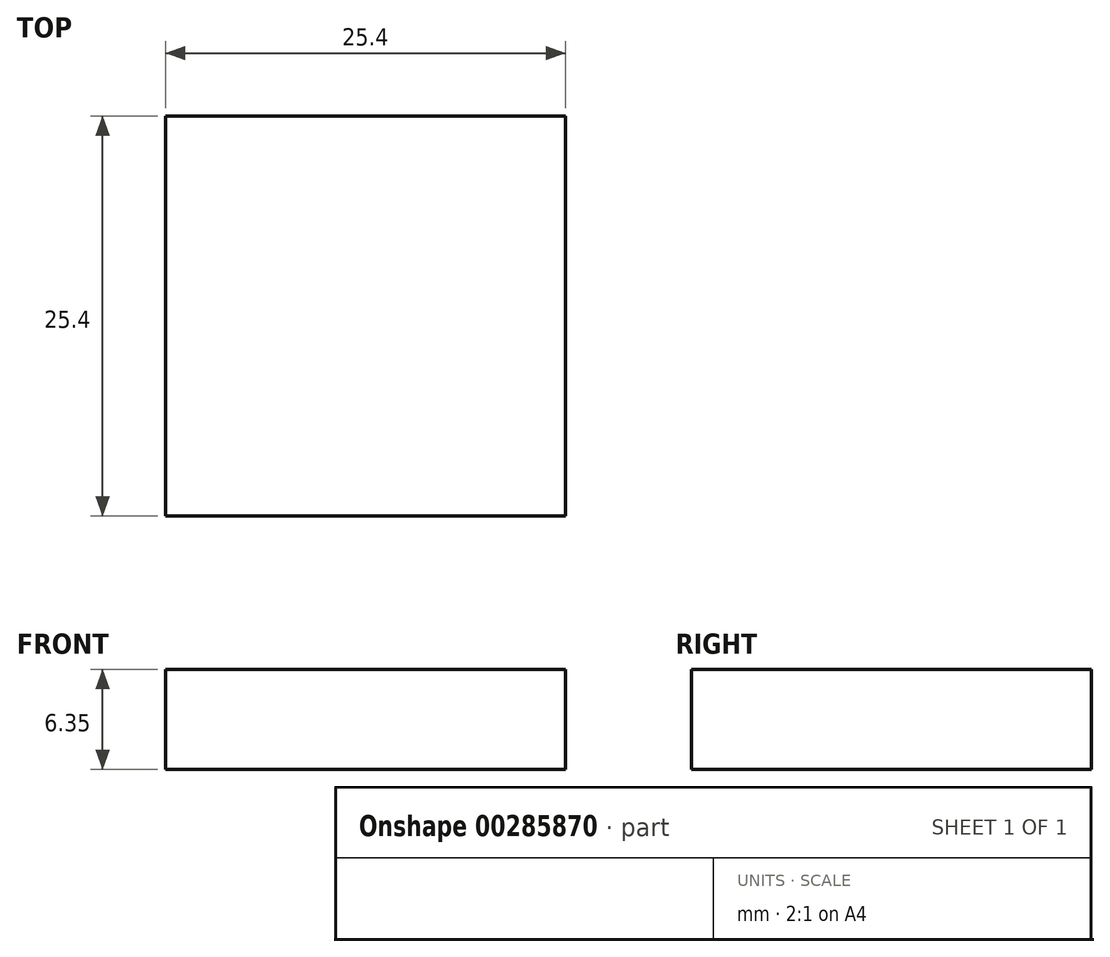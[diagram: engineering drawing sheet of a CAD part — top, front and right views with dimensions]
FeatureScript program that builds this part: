
annotation { "Feature Type Name" : "Feature", "Feature Type Description" : "" }
export const myFeature = defineFeature(function(context is Context, id is Id, definition is map)
    precondition{}
    {
        {
            var Q0;
            Q0=qCreatedBy(makeId("Top.planeOp"),FACE);
            var sketch = newSketch(context, id + "F0", { "sketchPlane" : qUnion([Q0])});
            skLineSegment(sketch, "E0.bottom", {"start": v(0, 0) * mm, "end": v(25.4, 0) * mm});
            skLineSegment(sketch, "E0.top", {"start": v(0, -25.4) * mm, "end": v(25.4, -25.4) * mm});
            skLineSegment(sketch, "E0.left", {"start": v(0, 0) * mm, "end": v(0, -25.4) * mm});
            skLineSegment(sketch, "E0.right", {"start": v(25.4, 0) * mm, "end": v(25.4, -25.4) * mm});
            skSolve(sketch);
        }
        {
            var Q0;
            Q0=makeQuery(id+"F0.imprint","IMPRINT",FACE,{"disambiguationData":[TD([[makeQuery(id+"F0.imprint","IMPRINT",EDGE,{"derivedFrom":sQuery(id+"F0.wireOp",EDGE,"E0.bottom")}),-1.0]])]});
            extrude(context, id + "F1", {"entities" : qUnion([Q0]), "depth" : 6.35 * mm});
        }
    });
